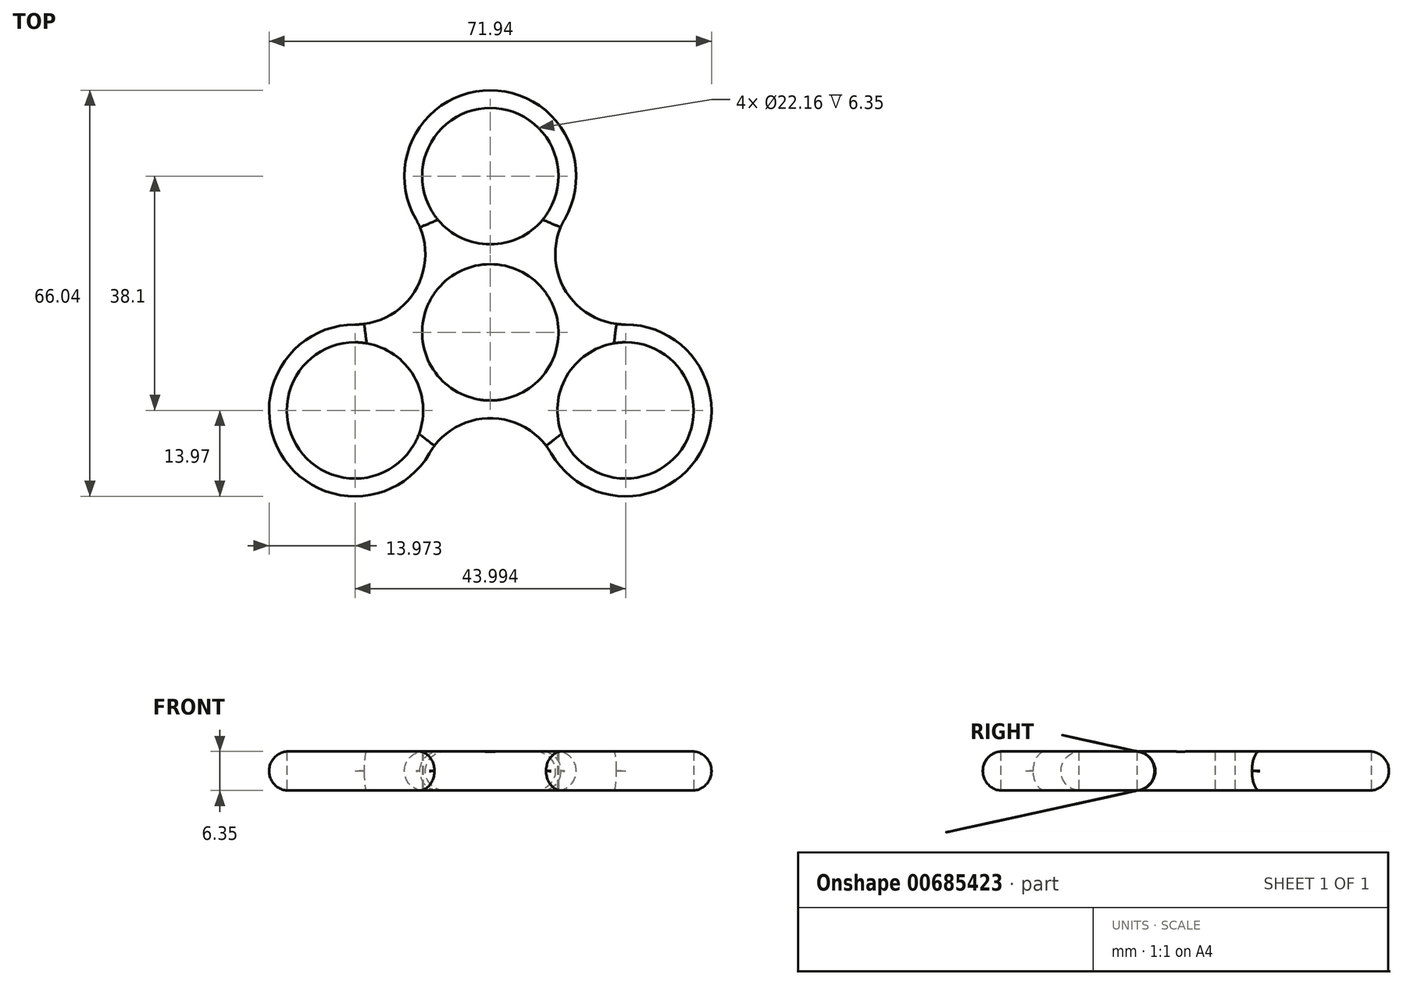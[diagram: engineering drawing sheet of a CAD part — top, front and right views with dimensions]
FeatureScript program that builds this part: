
annotation { "Feature Type Name" : "Feature", "Feature Type Description" : "" }
export const myFeature = defineFeature(function(context is Context, id is Id, definition is map)
    precondition{}
    {
        {
            var Q0;
            Q0=qCreatedBy(makeId("Top.planeOp"),FACE);
            var sketch = newSketch(context, id + "F0", { "sketchPlane" : qUnion([Q0])});
            skCircle(sketch, "E0", {"center": v(0, 0) * mm, "radius": 11.08 * mm});
            skCircle(sketch, "E1", {"center": v(0, 0) * mm, "radius": 13.97 * mm});
            skLineSegment(sketch, "E2", {"start": v(0, 0) * mm, "end": v(0, 25.4) * mm});
            skCircle(sketch, "E3", {"center": v(0, 25.4) * mm, "radius": 11.08 * mm});
            skCircle(sketch, "E4", {"center": v(0, 25.4) * mm, "radius": 13.97 * mm});
            skCircle(sketch, "E5.1.0", {"center": v(-22, -12.7) * mm, "radius": 11.08 * mm});
            skCircle(sketch, "E5.1.1", {"center": v(-22, -12.7) * mm, "radius": 13.97 * mm});
            skCircle(sketch, "E5.2.0", {"center": v(22, -12.7) * mm, "radius": 11.08 * mm});
            skCircle(sketch, "E5.2.1", {"center": v(22, -12.7) * mm, "radius": 13.97 * mm});
            skLineSegment(sketch, "E6", {"start": v(0, 0) * mm, "end": v(22, 12.7) * mm});
            skArc(sketch, "E7", {"start": v(12.1, 18.42) * mm, "mid": v(12.1, 6.99) * mm, "end": v(22, 1.27) * mm});
            skArc(sketch, "E8.1.0", {"start": v(-22, 1.27) * mm, "mid": v(-12.1, 6.99) * mm, "end": v(-12.1, 18.41) * mm});
            skArc(sketch, "E8.2.0", {"start": v(9.9, -19.69) * mm, "mid": v(0, -13.97) * mm, "end": v(-9.9, -19.68) * mm});
            skSolve(sketch);
        }
        {
            var Q0;
            Q0 = qSketchRegion(id + "F0", true);
            var Q1;
            {var subQ0=sQuery(id+"F0.wireOp",EDGE,"E2");var subQ1=sQuery(id+"F0.wireOp",EDGE,"E1");var subQ2=makeQuery(id+"F0.imprint","INTERSECT",VERTEX,{"derivedFrom":[subQ1,subQ0]});Q1=makeQuery(id+"F0.imprint","IMPRINT",FACE,{"disambiguationData":[TD([[makeQuery(id+"F0.imprint","IMPRINT",EDGE,{"disambiguationData":[TD([[subQ2,1.0]])],"derivedFrom":subQ1}),1.0]])]});}
            var Q2;
            {var subQ0=sQuery(id+"F0.wireOp",EDGE,"E5.2.1");var subQ1=sQuery(id+"F0.wireOp",EDGE,"E1");var subQ2=makeQuery(id+"F0.imprint","INTERSECT",VERTEX,{"disambiguationData":[OD(0.0)],"derivedFrom":[subQ1,subQ0]});Q2=makeQuery(id+"F0.imprint","IMPRINT",FACE,{"disambiguationData":[TD([[makeQuery(id+"F0.imprint","IMPRINT",EDGE,{"disambiguationData":[TD([[subQ2,-1.0]])],"derivedFrom":subQ1}),1.0]])]});}
            var Q3;
            {var subQ0=sQuery(id+"F0.wireOp",EDGE,"E5.1.1");var subQ1=sQuery(id+"F0.wireOp",EDGE,"E1");var subQ2=makeQuery(id+"F0.imprint","INTERSECT",VERTEX,{"disambiguationData":[OD(0.0)],"derivedFrom":[subQ1,subQ0]});Q3=makeQuery(id+"F0.imprint","IMPRINT",FACE,{"disambiguationData":[TD([[makeQuery(id+"F0.imprint","IMPRINT",EDGE,{"disambiguationData":[TD([[subQ2,-1.0]])],"derivedFrom":subQ1}),1.0]])]});}
            var Q4;
            {var subQ0=sQuery(id+"F0.wireOp",EDGE,"E2");var subQ1=sQuery(id+"F0.wireOp",EDGE,"E1");var subQ2=makeQuery(id+"F0.imprint","INTERSECT",VERTEX,{"derivedFrom":[subQ1,subQ0]});Q4=makeQuery(id+"F0.imprint","IMPRINT",FACE,{"disambiguationData":[TD([[makeQuery(id+"F0.imprint","IMPRINT",EDGE,{"disambiguationData":[TD([[subQ2,-1.0]])],"derivedFrom":subQ1}),1.0]])]});}
            extrude(context, id + "F1", {"entities" : qUnion([Q0, Q1, Q2, Q3, Q4]), "depth" : 6.35 * mm, "offsetDistance" : 25.4 * mm});
        }
        {
            var Q0;
            Q0=makeQuery(id+"F1.opExtrude","CAP_EDGE",EDGE,{"disambiguationData":[OSD([sQuery(id+"F0.wireOp",EDGE,"E5.1.1")])],"isStart":false});
            var Q1;
            Q1=makeQuery(id+"F1.opExtrude","CAP_EDGE",EDGE,{"disambiguationData":[OSD([sQuery(id+"F0.wireOp",EDGE,"E5.1.1")])],"isStart":true});
            fillet(context, id + "F2", {"entities" : qUnion([Q0, Q1]), "radius" : 3.17 * mm, "tangentPropagation" : true, "allowEdgeOverflow" : false});
        }
    });
